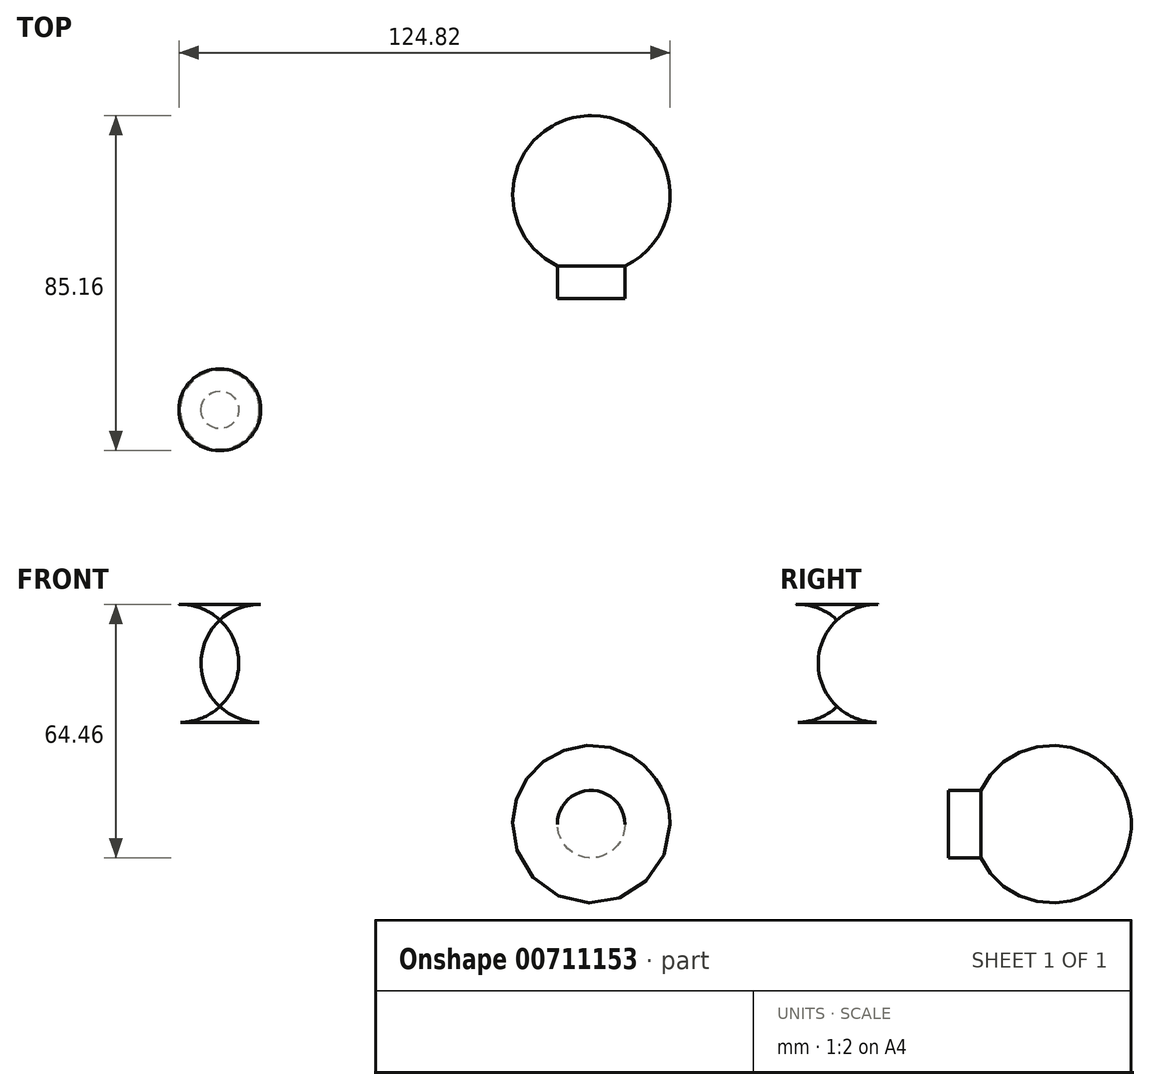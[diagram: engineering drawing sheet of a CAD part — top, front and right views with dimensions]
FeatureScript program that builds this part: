
annotation { "Feature Type Name" : "Feature", "Feature Type Description" : "" }
export const myFeature = defineFeature(function(context is Context, id is Id, definition is map)
    precondition{}
    {
        {
            var Q0;
            Q0=qCreatedBy(makeId("Top.planeOp"),FACE);
            var sketch = newSketch(context, id + "F0", { "sketchPlane" : qUnion([Q0])});
            skLineSegment(sketch, "E0.top", {"start": v(33.77, 28.26) * mm, "end": v(42.34, 28.26) * mm});
            skLineSegment(sketch, "E0.left", {"start": v(33.77, 54.66) * mm, "end": v(33.77, 28.26) * mm});
            skLineSegment(sketch, "E1.right", {"start": v(33.85, 54.66) * mm, "end": v(33.85, 74.75) * mm});
            skLineSegment(sketch, "E2.right", {"start": v(33.77, 54.66) * mm, "end": v(33.77, 34.56) * mm});
            skLineSegment(sketch, "E3", {"start": v(33.77, 28.26) * mm, "end": v(33.77, 34.56) * mm});
            skArc(sketch, "E4", {"start": v(33.77, 34.56) * mm, "mid": v(53.85, 54.61) * mm, "end": v(33.85, 74.75) * mm});
            skLineSegment(sketch, "E5", {"start": v(33.85, 74.75) * mm, "end": v(33.77, 28.26) * mm});
            skLineSegment(sketch, "E6", {"start": v(42.34, 28.26) * mm, "end": v(42.34, 36.49) * mm});
            skSolve(sketch);
        }
        {
            var Q0;
            {var subQ0=sQuery(id+"F0.wireOp",EDGE,"E4");var subQ1=makeQuery(id+"F0.imprint","INTERSECT",VERTEX,{"derivedFrom":[subQ0,sQuery(id+"F0.wireOp",EDGE,"E6")]});Q0=makeQuery(id+"F0.imprint","IMPRINT",FACE,{"disambiguationData":[TD([[makeQuery(id+"F0.imprint","IMPRINT",EDGE,{"disambiguationData":[TD([[subQ1,1.0]])],"derivedFrom":subQ0}),1.0]])]});}
            var Q1;
            {var subQ4=sQuery(id+"F0.wireOp",EDGE,"E0.top");Q1=makeQuery(id+"F0.imprint","IMPRINT",FACE,{"disambiguationData":[TD([[makeQuery(id+"F0.imprint","IMPRINT",EDGE,{"derivedFrom":subQ4}),1.0]])]});}
            var Q2;
            Q2=sQuery(id+"F0.wireOp",EDGE,"E5");
            revolve(context, id + "F1", {"surfaceOperationType" : NewSurfaceOperationType.NEW, "entities" : qUnion([Q0, Q1]), "axis" : qUnion([Q2]), "revolveType" : RevolveType.FULL});
        }
        {
            var Q0;
            Q0=qCreatedBy(makeId("Front.planeOp"),FACE);
            var sketch = newSketch(context, id + "F2", { "sketchPlane" : qUnion([Q0])});
            skLineSegment(sketch, "E7", {"start": v(-60.57, 55.87) * mm, "end": v(-60.57, 25.87) * mm});
            skLineSegment(sketch, "E8", {"start": v(-60.57, 25.87) * mm, "end": v(-50.57, 25.87) * mm});
            skArc(sketch, "E9", {"start": v(-50.57, 25.87) * mm, "mid": v(-35.37, 40.67) * mm, "end": v(-50.16, 55.87) * mm});
            skLineSegment(sketch, "E10", {"start": v(-50.16, 55.87) * mm, "end": v(-60.57, 55.87) * mm});
            skSolve(sketch);
        }
        {
            var Q0;
            Q0=makeQuery(id+"F2.imprint","IMPRINT",FACE,{"disambiguationData":[TD([[makeQuery(id+"F2.imprint","IMPRINT",EDGE,{"derivedFrom":sQuery(id+"F2.wireOp",EDGE,"E7")}),1.0]])]});
            var Q1;
            Q1=sQuery(id+"F2.wireOp",EDGE,"E7");
            revolve(context, id + "F3", {"surfaceOperationType" : NewSurfaceOperationType.NEW, "entities" : qUnion([Q0]), "axis" : qUnion([Q1]), "revolveType" : RevolveType.FULL});
        }
    });
